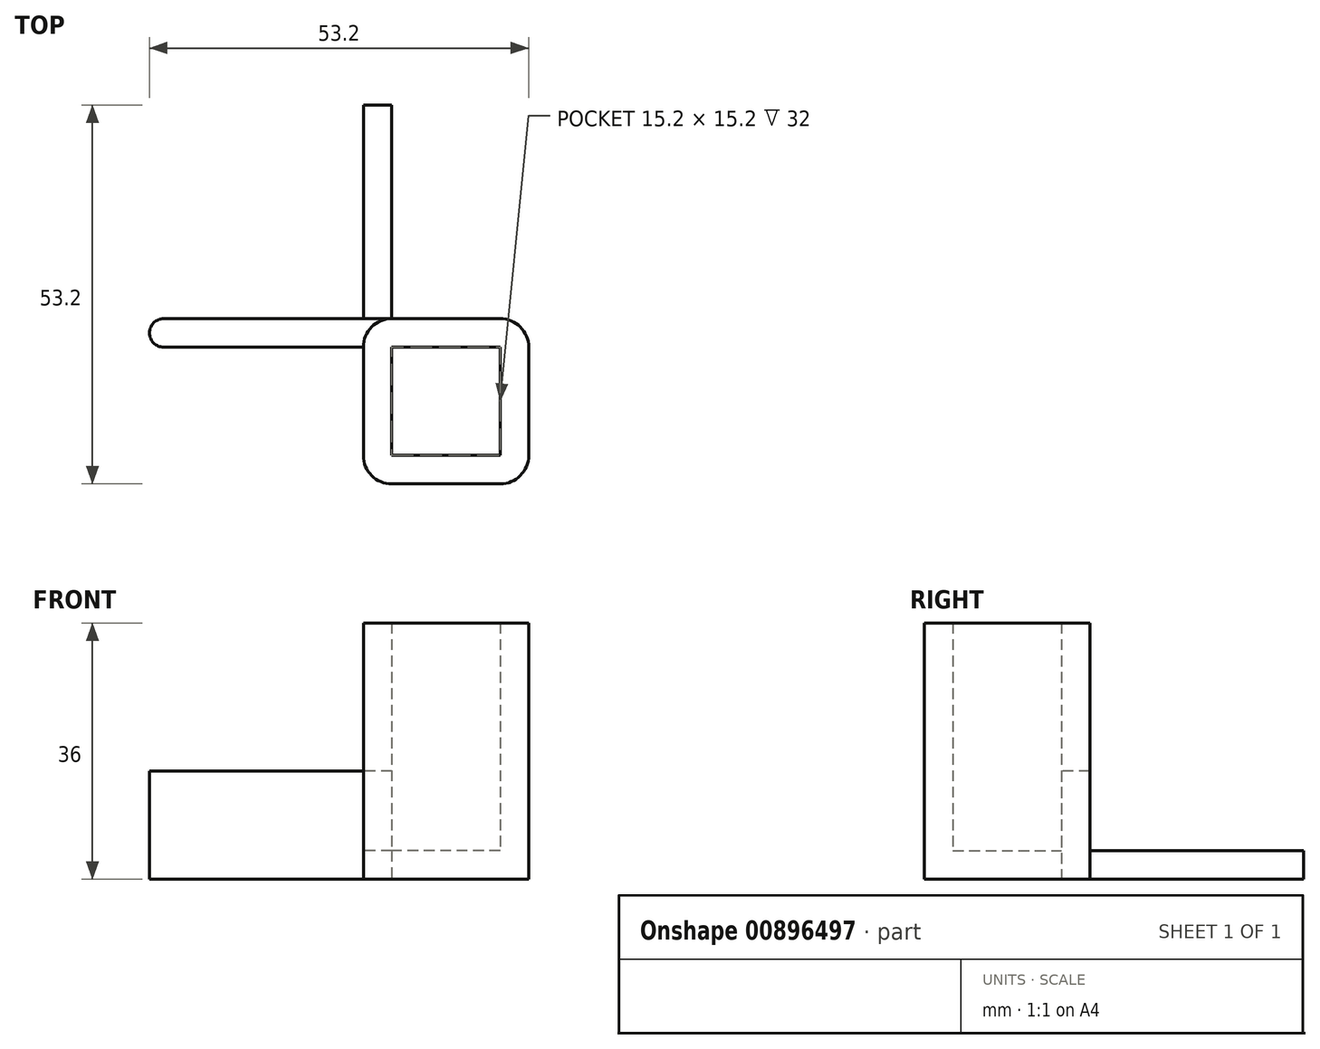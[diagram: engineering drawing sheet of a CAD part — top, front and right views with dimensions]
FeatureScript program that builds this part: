
annotation { "Feature Type Name" : "Feature", "Feature Type Description" : "" }
export const myFeature = defineFeature(function(context is Context, id is Id, definition is map)
    precondition{}
    {
        {
            var Q0;
            Q0=qCreatedBy(makeId("Top.planeOp"),FACE);
            var sketch = newSketch(context, id + "F0", { "sketchPlane" : qUnion([Q0])});
            skLineSegment(sketch, "E0.bottom", {"start": v(0, 15.2) * mm, "end": v(15.2, 15.2) * mm});
            skLineSegment(sketch, "E0.top", {"start": v(0, 0) * mm, "end": v(15.2, 0) * mm});
            skLineSegment(sketch, "E0.left", {"start": v(0, 15.2) * mm, "end": v(0, 0) * mm});
            skLineSegment(sketch, "E0.right", {"start": v(15.2, 15.2) * mm, "end": v(15.2, 0) * mm});
            skLineSegment(sketch, "E1.bottom", {"start": v(-4, -4) * mm, "end": v(19.2, -4) * mm});
            skLineSegment(sketch, "E1.top", {"start": v(-4, 19.2) * mm, "end": v(19.2, 19.2) * mm});
            skLineSegment(sketch, "E1.left", {"start": v(-4, -4) * mm, "end": v(-4, 19.2) * mm});
            skLineSegment(sketch, "E1.right", {"start": v(19.2, -4) * mm, "end": v(19.2, 19.2) * mm});
            skLineSegment(sketch, "E2", {"start": v(7.6, -4) * mm, "end": v(7.6, 0) * mm, "construction": true});
            skLineSegment(sketch, "E3", {"start": v(-4, 7.6) * mm, "end": v(0, 7.6) * mm, "construction": true});
            skLineSegment(sketch, "E4.bottom", {"start": v(-4, 15.2) * mm, "end": v(-34, 15.2) * mm});
            skLineSegment(sketch, "E4.top", {"start": v(-4, 19.2) * mm, "end": v(-34, 19.2) * mm});
            skLineSegment(sketch, "E4.left", {"start": v(-4, 15.2) * mm, "end": v(-4, 19.2) * mm});
            skLineSegment(sketch, "E4.right", {"start": v(-34, 15.2) * mm, "end": v(-34, 19.2) * mm});
            skLineSegment(sketch, "E5.bottom", {"start": v(-4, 19.2) * mm, "end": v(0, 19.2) * mm});
            skLineSegment(sketch, "E5.top", {"start": v(-4, 49.2) * mm, "end": v(0, 49.2) * mm});
            skLineSegment(sketch, "E5.left", {"start": v(-4, 19.2) * mm, "end": v(-4, 49.2) * mm});
            skLineSegment(sketch, "E5.right", {"start": v(0, 19.2) * mm, "end": v(0, 49.2) * mm});
            skSolve(sketch);
        }
        {
            var Q0;
            Q0 = qSketchRegion(id + "F0", true);
            var Q1;
            Q1=makeQuery(id+"F0.imprint","IMPRINT",FACE,{"disambiguationData":[TD([[makeQuery(id+"F0.imprint","IMPRINT",EDGE,{"derivedFrom":sQuery(id+"F0.wireOp",EDGE,"E0.bottom")}),-1.0]])]});
            extrude(context, id + "F1", {"entities" : qUnion([Q0, Q1]), "depth" : 4 * mm, "offsetDistance" : 25 * mm});
        }
        {
            var Q0;
            Q0=makeQuery(id+"F0.imprint","IMPRINT",FACE,{"disambiguationData":[TD([[makeQuery(id+"F0.imprint","IMPRINT",EDGE,{"derivedFrom":sQuery(id+"F0.wireOp",EDGE,"E0.bottom")}),1.0]])]});
            extrude(context, id + "F2", {"entities" : qUnion([Q0]), "operationType" : NewBodyOperationType.ADD, "depth" : 36 * mm, "offsetDistance" : 25 * mm});
        }
        {
            var Q0;
            Q0=makeQuery(id+"F0.imprint","IMPRINT",FACE,{"disambiguationData":[TD([[makeQuery(id+"F0.imprint","IMPRINT",EDGE,{"derivedFrom":sQuery(id+"F0.wireOp",EDGE,"E4.bottom")}),-1.0]])]});
            var Q1;
            Q1=makeQuery(id+"F0.imprint","IMPRINT",FACE,{"disambiguationData":[TD([[makeQuery(id+"F0.imprint","IMPRINT",EDGE,{"derivedFrom":sQuery(id+"F0.wireOp",EDGE,"E5.bottom")}),1.0]])]});
            extrude(context, id + "F3", {"entities" : qUnion([Q0, Q1]), "operationType" : NewBodyOperationType.ADD, "depth" : 15.2 * mm, "offsetDistance" : 25 * mm});
        }
        {
            var Q0;
            {var subQ0=sQuery(id+"F0.wireOp",EDGE,"E1.left");var subQ1=sQuery(id+"F0.wireOp",EDGE,"E1.bottom");Q0=makeQuery(id+"F2.boolean.opBoolean","MERGE",EDGE,{"derivedFrom":[makeQuery(id+"F1.opExtrude","SWEPT_EDGE",EDGE,{"disambiguationData":[OSD([subQ1,subQ0])]}),makeQuery(id+"F2.opExtrude","SWEPT_EDGE",EDGE,{"disambiguationData":[OSD([subQ1,subQ0])]})]});}
            var Q1;
            {var subQ0=sQuery(id+"F0.wireOp",EDGE,"E1.right");var subQ1=sQuery(id+"F0.wireOp",EDGE,"E1.bottom");Q1=makeQuery(id+"F2.boolean.opBoolean","MERGE",EDGE,{"derivedFrom":[makeQuery(id+"F1.opExtrude","SWEPT_EDGE",EDGE,{"disambiguationData":[OSD([subQ1,subQ0])]}),makeQuery(id+"F2.opExtrude","SWEPT_EDGE",EDGE,{"disambiguationData":[OSD([subQ1,subQ0])]})]});}
            var Q2;
            {var subQ0=sQuery(id+"F0.wireOp",EDGE,"E1.right");var subQ1=sQuery(id+"F0.wireOp",EDGE,"E1.top");Q2=makeQuery(id+"F2.boolean.opBoolean","MERGE",EDGE,{"derivedFrom":[makeQuery(id+"F1.opExtrude","SWEPT_EDGE",EDGE,{"disambiguationData":[OSD([subQ1,subQ0])]}),makeQuery(id+"F2.opExtrude","SWEPT_EDGE",EDGE,{"disambiguationData":[OSD([subQ1,subQ0])]})]});}
            var Q3;
            {var subQ0=sQuery(id+"F0.wireOp",EDGE,"E5.left");var subQ1=sQuery(id+"F0.wireOp",EDGE,"E5.bottom");var subQ2=sQuery(id+"F0.wireOp",EDGE,"E4.left");var subQ3=sQuery(id+"F0.wireOp",EDGE,"E4.top");Q3=makeQuery(id+"F2.boolean.opBoolean","MERGE",EDGE,{"derivedFrom":[makeQuery(id+"F1.opExtrude","SWEPT_EDGE",EDGE,{"disambiguationData":[OSD([subQ3,subQ2,subQ1,subQ0])]}),makeQuery(id+"F2.opExtrude","SWEPT_EDGE",EDGE,{"disambiguationData":[OSD([subQ3,subQ2,subQ1,subQ0])]})]});}
            var Q4;
            {var subQ0=sQuery(id+"F0.wireOp",EDGE,"E5.left");var subQ1=sQuery(id+"F0.wireOp",EDGE,"E5.bottom");var subQ2=sQuery(id+"F0.wireOp",EDGE,"E4.left");var subQ3=sQuery(id+"F0.wireOp",EDGE,"E4.top");Q4=makeQuery(id+"F3.boolean.opBoolean","MERGE",EDGE,{"derivedFrom":[makeQuery(id+"F1.opExtrude","SWEPT_EDGE",EDGE,{"disambiguationData":[OSD([subQ3,subQ2,subQ1,subQ0])]}),makeQuery(id+"F3.opExtrude","SWEPT_EDGE",EDGE,{"disambiguationData":[OSD([subQ3,subQ2,subQ1,subQ0]),OD(0.0)]})]});}
            fillet(context, id + "F4", {"entities" : qUnion([Q0, Q1, Q2, Q3, Q4]), "radius" : 4 * mm, "tangentPropagation" : true, "allowEdgeOverflow" : false});
        }
        {
            var Q0;
            Q0=makeQuery(id+"F2.opExtrude","SWEPT_EDGE",EDGE,{"disambiguationData":[OSD([sQuery(id+"F0.wireOp",EDGE,"E4.top"),sQuery(id+"F0.wireOp",EDGE,"E4.left"),sQuery(id+"F0.wireOp",EDGE,"E5.bottom"),sQuery(id+"F0.wireOp",EDGE,"E5.left")])]});
            fillet(context, id + "F5", {"entities" : qUnion([Q0]), "radius" : 4 * mm, "tangentPropagation" : true, "allowEdgeOverflow" : false});
        }
        {
            var Q0;
            {var subQ0=sQuery(id+"F0.wireOp",EDGE,"E5.right");var subQ1=sQuery(id+"F0.wireOp",EDGE,"E5.top");Q0=makeQuery(id+"F3.boolean.opBoolean","MERGE",EDGE,{"derivedFrom":[makeQuery(id+"F1.opExtrude","SWEPT_EDGE",EDGE,{"disambiguationData":[OSD([subQ1,subQ0])]}),makeQuery(id+"F3.opExtrude","SWEPT_EDGE",EDGE,{"disambiguationData":[OSD([subQ1,subQ0])]})]});}
            var Q1;
            {var subQ0=sQuery(id+"F0.wireOp",EDGE,"E5.left");var subQ1=sQuery(id+"F0.wireOp",EDGE,"E5.top");Q1=makeQuery(id+"F3.boolean.opBoolean","MERGE",EDGE,{"derivedFrom":[makeQuery(id+"F1.opExtrude","SWEPT_EDGE",EDGE,{"disambiguationData":[OSD([subQ1,subQ0])]}),makeQuery(id+"F3.opExtrude","SWEPT_EDGE",EDGE,{"disambiguationData":[OSD([subQ1,subQ0])]})]});}
            var Q2;
            {var subQ0=sQuery(id+"F0.wireOp",EDGE,"E4.right");var subQ1=sQuery(id+"F0.wireOp",EDGE,"E4.top");Q2=makeQuery(id+"F3.boolean.opBoolean","MERGE",EDGE,{"derivedFrom":[makeQuery(id+"F1.opExtrude","SWEPT_EDGE",EDGE,{"disambiguationData":[OSD([subQ1,subQ0])]}),makeQuery(id+"F3.opExtrude","SWEPT_EDGE",EDGE,{"disambiguationData":[OSD([subQ1,subQ0])]})]});}
            var Q3;
            {var subQ0=sQuery(id+"F0.wireOp",EDGE,"E4.right");var subQ1=sQuery(id+"F0.wireOp",EDGE,"E4.bottom");Q3=makeQuery(id+"F3.boolean.opBoolean","MERGE",EDGE,{"derivedFrom":[makeQuery(id+"F1.opExtrude","SWEPT_EDGE",EDGE,{"disambiguationData":[OSD([subQ1,subQ0])]}),makeQuery(id+"F3.opExtrude","SWEPT_EDGE",EDGE,{"disambiguationData":[OSD([subQ1,subQ0])]})]});}
            fillet(context, id + "F6", {"entities" : qUnion([Q0, Q1, Q2, Q3]), "radius" : 2 * mm, "tangentPropagation" : true, "allowEdgeOverflow" : false});
        }
    });
